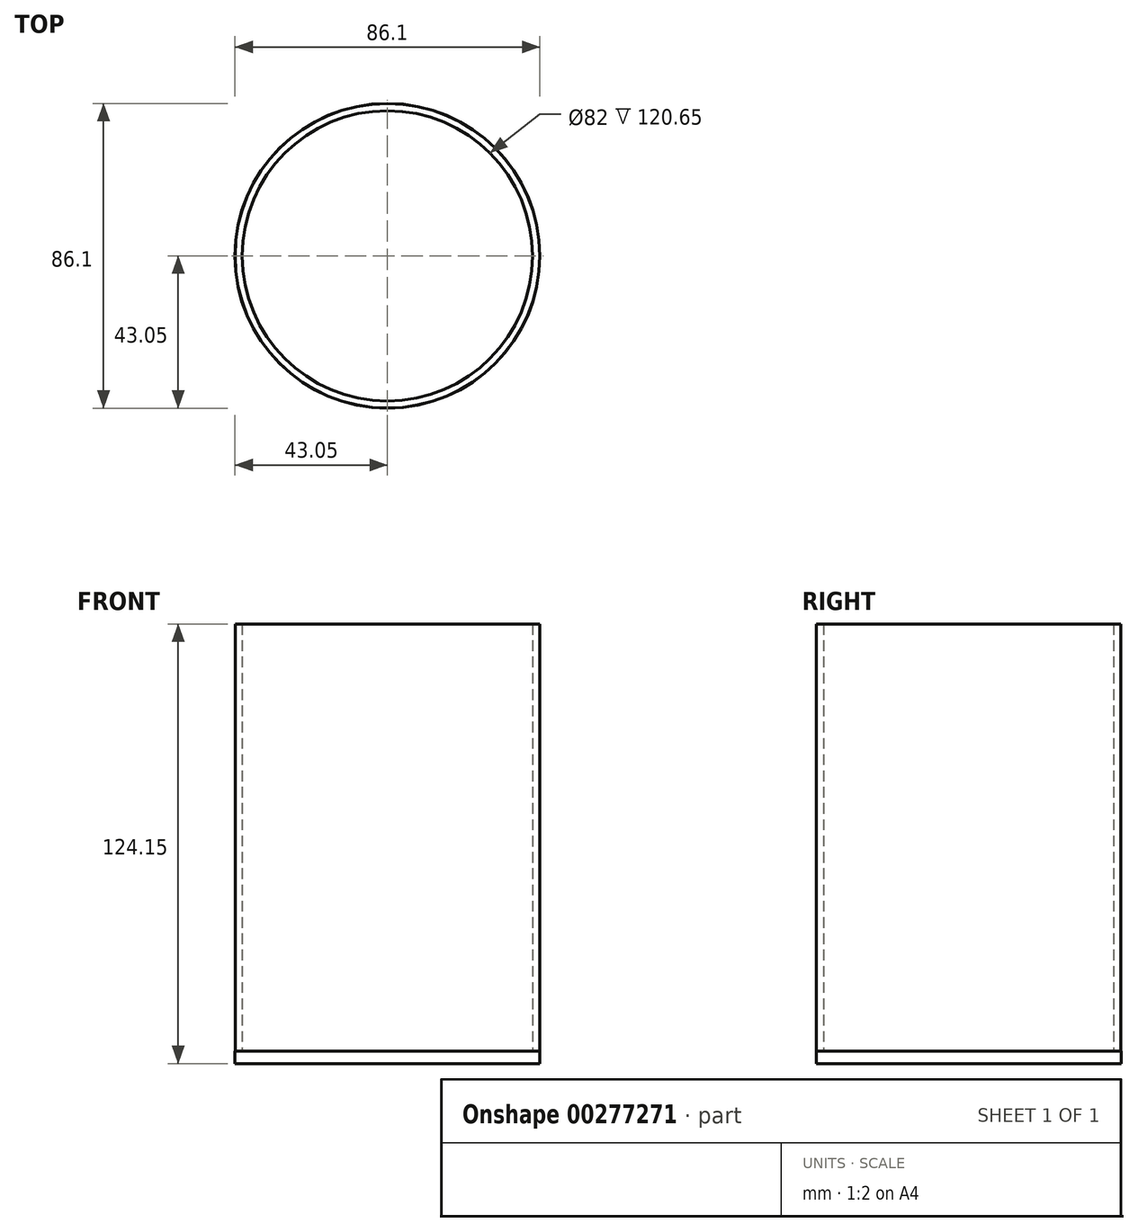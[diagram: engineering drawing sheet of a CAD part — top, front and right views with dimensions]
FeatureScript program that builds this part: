
annotation { "Feature Type Name" : "Feature", "Feature Type Description" : "" }
export const myFeature = defineFeature(function(context is Context, id is Id, definition is map)
    precondition{}
    {
        {
            var Q0;
            Q0=qCreatedBy(makeId("Top.planeOp"),FACE);
            var sketch = newSketch(context, id + "F2", { "sketchPlane" : qUnion([Q0])});
            skCircle(sketch, "E0", {"center": v(0, 0) * mm, "radius": 41 * mm});
            skCircle(sketch, "E1.0", {"center": v(0, 0) * mm, "radius": 43 * mm});
            skSolve(sketch);
        }
        {
            var Q0;
            Q0=makeQuery(id+"F2.imprint","IMPRINT",FACE,{"disambiguationData":[TD([[makeQuery(id+"F2.imprint","IMPRINT",EDGE,{"derivedFrom":sQuery(id+"F2.wireOp",EDGE,"E0")}),-1.0]])]});
            extrude(context, id + "F0", {"entities" : qUnion([Q0]), "depth" : 120.65 * mm});
        }
        {
            var Q0;
            Q0=qCreatedBy(makeId("Top.planeOp"),FACE);
            var sketch = newSketch(context, id + "F3", { "sketchPlane" : qUnion([Q0])});
            skCircle(sketch, "E2", {"center": v(0, 0) * mm, "radius": 43.05 * mm});
            skSolve(sketch);
        }
        {
            var Q0;
            Q0=makeQuery(id+"F3.imprint","IMPRINT",FACE,{"disambiguationData":[TD([[makeQuery(id+"F3.imprint","IMPRINT",EDGE,{"derivedFrom":sQuery(id+"F3.wireOp",EDGE,"E2")}),1.0]])]});
            extrude(context, id + "F1", {"entities" : qUnion([Q0]), "operationType" : NewBodyOperationType.ADD, "oppositeDirection" : true, "depth" : 3.5 * mm});
        }
    });
